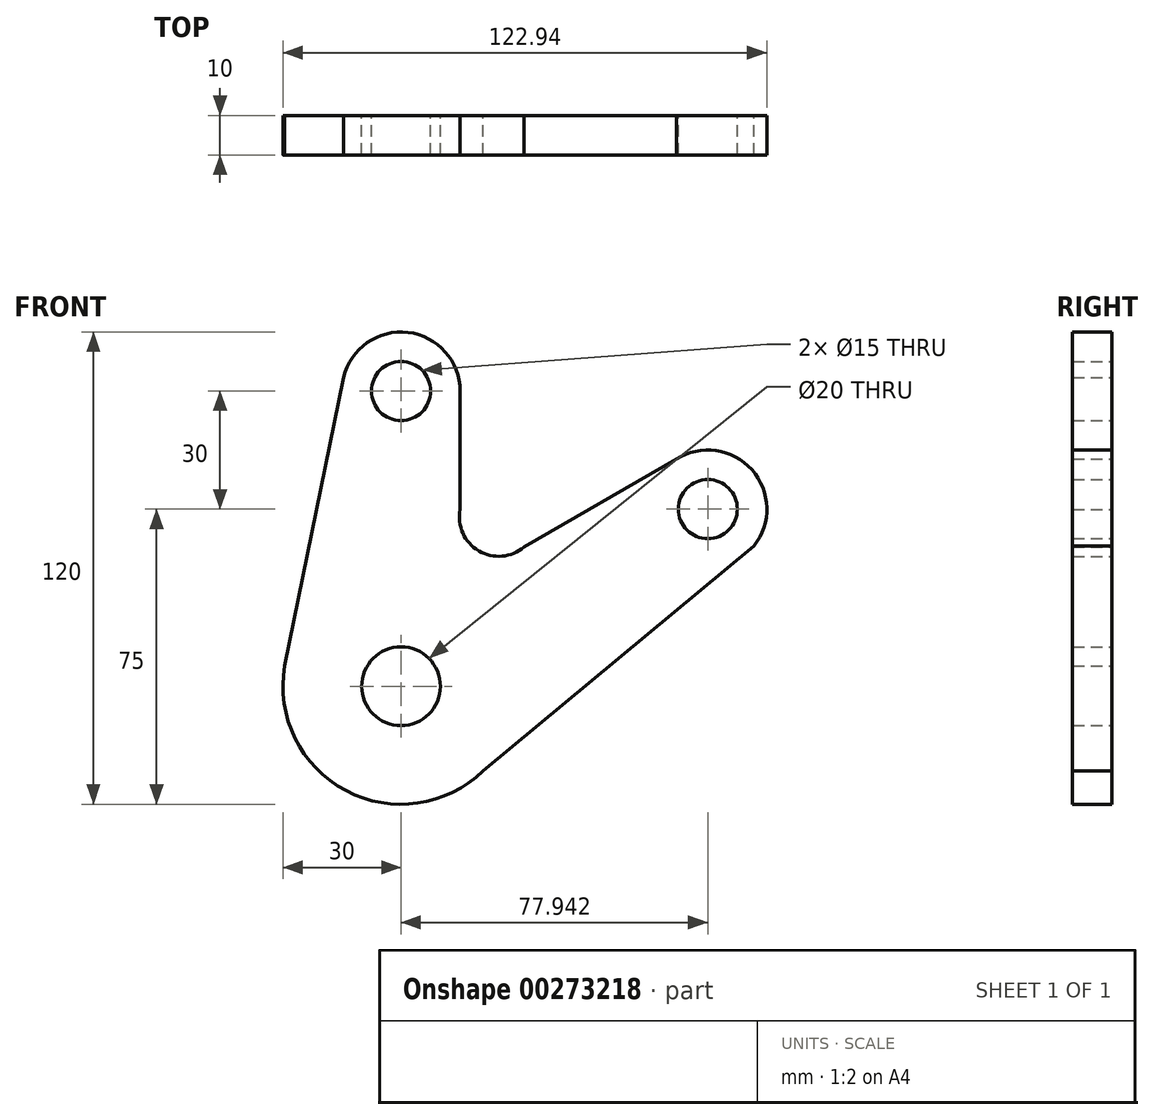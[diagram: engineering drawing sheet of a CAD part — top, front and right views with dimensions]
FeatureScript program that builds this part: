
annotation { "Feature Type Name" : "Feature", "Feature Type Description" : "" }
export const myFeature = defineFeature(function(context is Context, id is Id, definition is map)
    precondition{}
    {
        {
            var Q0;
            Q0=qCreatedBy(makeId("Front.planeOp"),FACE);
            var sketch = newSketch(context, id + "F0", { "sketchPlane" : qUnion([Q0])});
            skLineSegment(sketch, "E0", {"start": v(0, 0) * mm, "end": v(0, 75) * mm, "construction": true});
            skLineSegment(sketch, "E1", {"start": v(0, 0) * mm, "end": v(77.94, 45) * mm, "construction": true});
            skCircle(sketch, "E2", {"center": v(0, 75) * mm, "radius": 7.5 * mm});
            skCircle(sketch, "E3", {"center": v(77.94, 45) * mm, "radius": 7.5 * mm});
            skCircle(sketch, "E4", {"center": v(0, 0) * mm, "radius": 10 * mm});
            skArc(sketch, "E5", {"start": v(20.88, -21.54) * mm, "mid": v(-14.03, -26.52) * mm, "end": v(-29.56, 5.14) * mm});
            skArc(sketch, "E6", {"start": v(-14.6, 78.48) * mm, "mid": v(1.75, 89.9) * mm, "end": v(15, 75) * mm});
            skArc(sketch, "E7", {"start": v(69.92, 57.68) * mm, "mid": v(89.12, 55) * mm, "end": v(89.66, 35.63) * mm});
            skLineSegment(sketch, "E8", {"start": v(-14.6, 78.48) * mm, "end": v(-29.56, 5.14) * mm});
            skLineSegment(sketch, "E9", {"start": v(89.66, 35.63) * mm, "end": v(20.88, -21.54) * mm});
            skArc(sketch, "E10", {"start": v(15, 44.9) * mm, "mid": v(19.75, 34.39) * mm, "end": v(31.25, 35.35) * mm});
            skLineSegment(sketch, "E11", {"start": v(15, 44.9) * mm, "end": v(15, 75) * mm});
            skLineSegment(sketch, "E12", {"start": v(31.25, 35.35) * mm, "end": v(69.92, 57.68) * mm});
            skSolve(sketch);
        }
        {
            var Q0;
            Q0 = qSketchRegion(id + "F0", true);
            extrude(context, id + "F1", {"entities" : qUnion([Q0]), "depth" : 10 * mm});
        }
    });
